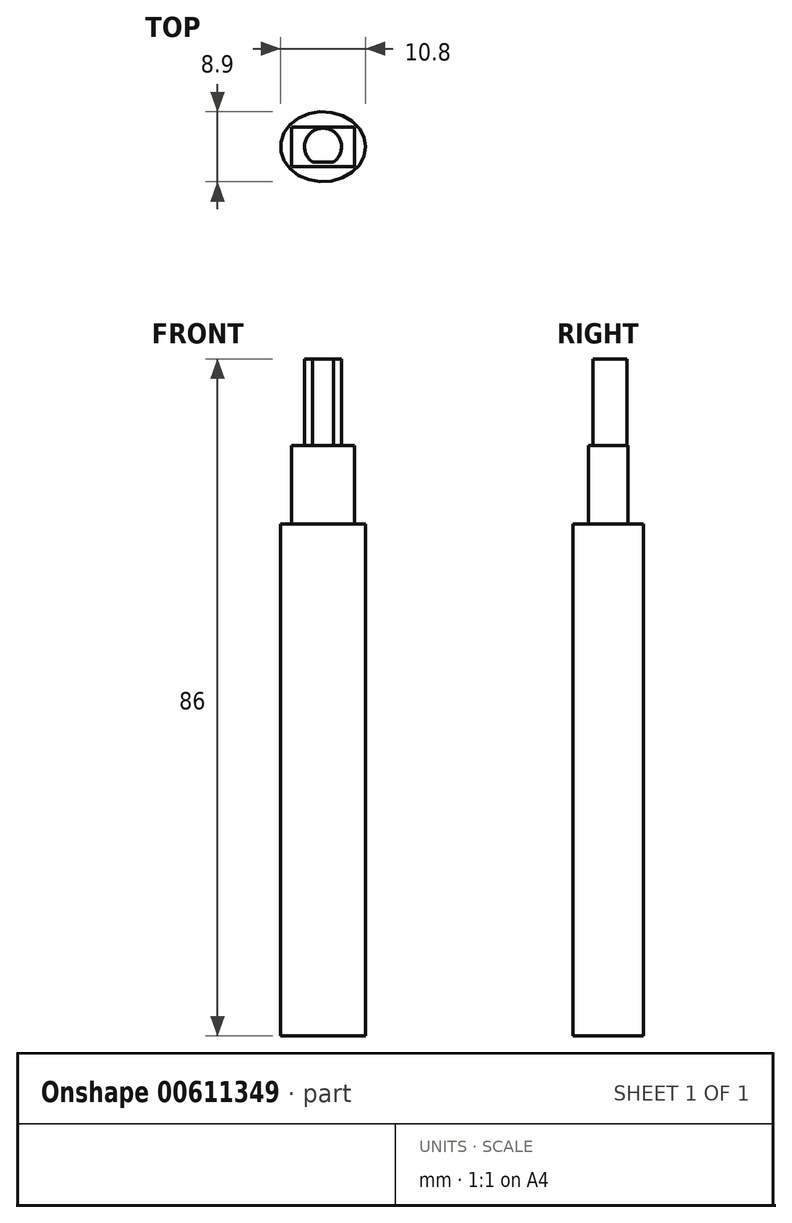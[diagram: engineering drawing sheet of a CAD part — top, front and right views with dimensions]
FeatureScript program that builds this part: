
annotation { "Feature Type Name" : "Feature", "Feature Type Description" : "" }
export const myFeature = defineFeature(function(context is Context, id is Id, definition is map)
    precondition{}
    {
        {
            var Q0;
            Q0=qCreatedBy(makeId("Top.planeOp"),FACE);
            var sketch = newSketch(context, id + "F0", { "sketchPlane" : qUnion([Q0])});
            skEllipse(sketch, "E0", {"center": v(0, 0) * mm, "majorRadius": 5.4 * mm, "minorRadius": 4.45 * mm, "majorAxis": v(1, 0)});
            skPoint(sketch, "E1", {"position": v(-5.4, 0) * mm});
            skPoint(sketch, "E2", {"position": v(0, -4.45) * mm});
            skPoint(sketch, "E3", {"position": v(5.4, 0) * mm});
            skPoint(sketch, "E4", {"position": v(0, 4.45) * mm});
            skSolve(sketch);
        }
        {
            var Q0;
            Q0=makeQuery(id+"F0.imprint","IMPRINT",FACE,{"disambiguationData":[TD([[makeQuery(id+"F0.imprint","IMPRINT",EDGE,{"derivedFrom":sQuery(id+"F0.wireOp",EDGE,"E0")}),1.0]])]});
            extrude(context, id + "F1", {"entities" : qUnion([Q0]), "depth" : 65 * mm, "offsetDistance" : 25 * mm});
        }
        {
            var Q0;
            Q0=makeQuery(id+"F1.opExtrude","CAP_FACE",FACE,{"disambiguationData":[OSD([sQuery(id+"F0.wireOp",EDGE,"E0")])],"isStart":false});
            var sketch = newSketch(context, id + "F2", { "sketchPlane" : qUnion([Q0])});
            skLineSegment(sketch, "E5.bottom", {"start": v(4, 2.5) * mm, "end": v(-4, 2.5) * mm});
            skLineSegment(sketch, "E5.top", {"start": v(4, -2.5) * mm, "end": v(-4, -2.5) * mm});
            skLineSegment(sketch, "E5.left", {"start": v(4, 2.5) * mm, "end": v(4, -2.5) * mm});
            skLineSegment(sketch, "E5.right", {"start": v(-4, 2.5) * mm, "end": v(-4, -2.5) * mm});
            skPoint(sketch, "E5.middle", {"position": v(0, 0) * mm});
            skSolve(sketch);
        }
        {
            var Q0;
            Q0=makeQuery(id+"F2.imprint","IMPRINT",FACE,{"disambiguationData":[TD([[makeQuery(id+"F2.imprint","IMPRINT",EDGE,{"derivedFrom":sQuery(id+"F2.wireOp",EDGE,"E5.bottom")}),1.0]])]});
            extrude(context, id + "F3", {"entities" : qUnion([Q0]), "operationType" : NewBodyOperationType.ADD, "depth" : 10 * mm, "offsetDistance" : 25 * mm});
        }
        {
            var Q0;
            Q0=makeQuery(id+"F3.opExtrude","CAP_FACE",FACE,{"disambiguationData":[OSD([sQuery(id+"F2.wireOp",EDGE,"E5.bottom"),sQuery(id+"F2.wireOp",EDGE,"E5.top"),sQuery(id+"F2.wireOp",EDGE,"E5.left"),sQuery(id+"F2.wireOp",EDGE,"E5.right")])],"isStart":false});
            var sketch = newSketch(context, id + "F4", { "sketchPlane" : qUnion([Q0])});
            skCircle(sketch, "E6", {"center": v(0, 0) * mm, "radius": 2.35 * mm});
            skSolve(sketch);
        }
        {
            var Q0;
            Q0 = qSketchRegion(id + "F4", true);
            extrude(context, id + "F5", {"entities" : qUnion([Q0]), "operationType" : NewBodyOperationType.ADD, "depth" : 11 * mm, "offsetDistance" : 25 * mm});
        }
        {
            var Q0;
            Q0=makeQuery(id+"F5.opExtrude","CAP_FACE",FACE,{"disambiguationData":[OSD([sQuery(id+"F4.wireOp",EDGE,"E6")])],"isStart":false});
            var sketch = newSketch(context, id + "F6", { "sketchPlane" : qUnion([Q0])});
            skLineSegment(sketch, "E7", {"start": v(0, -2.35) * mm, "end": v(0, -1.94) * mm});
            skLineSegment(sketch, "E8", {"start": v(0, -1.94) * mm, "end": v(-1.33, -1.94) * mm});
            skLineSegment(sketch, "E9", {"start": v(-1.33, -1.94) * mm, "end": v(1.33, -1.94) * mm});
            skArc(sketch, "E10", {"start": v(1.33, -1.94) * mm, "mid": v(0, -2.35) * mm, "end": v(-1.33, -1.94) * mm});
            skSolve(sketch);
        }
        {
            var Q0;
            Q0 = qSketchRegion(id + "F6", true);
            extrude(context, id + "F7", {"entities" : qUnion([Q0]), "operationType" : NewBodyOperationType.REMOVE, "oppositeDirection" : true, "depth" : 11 * mm, "offsetDistance" : 25 * mm});
        }
    });
